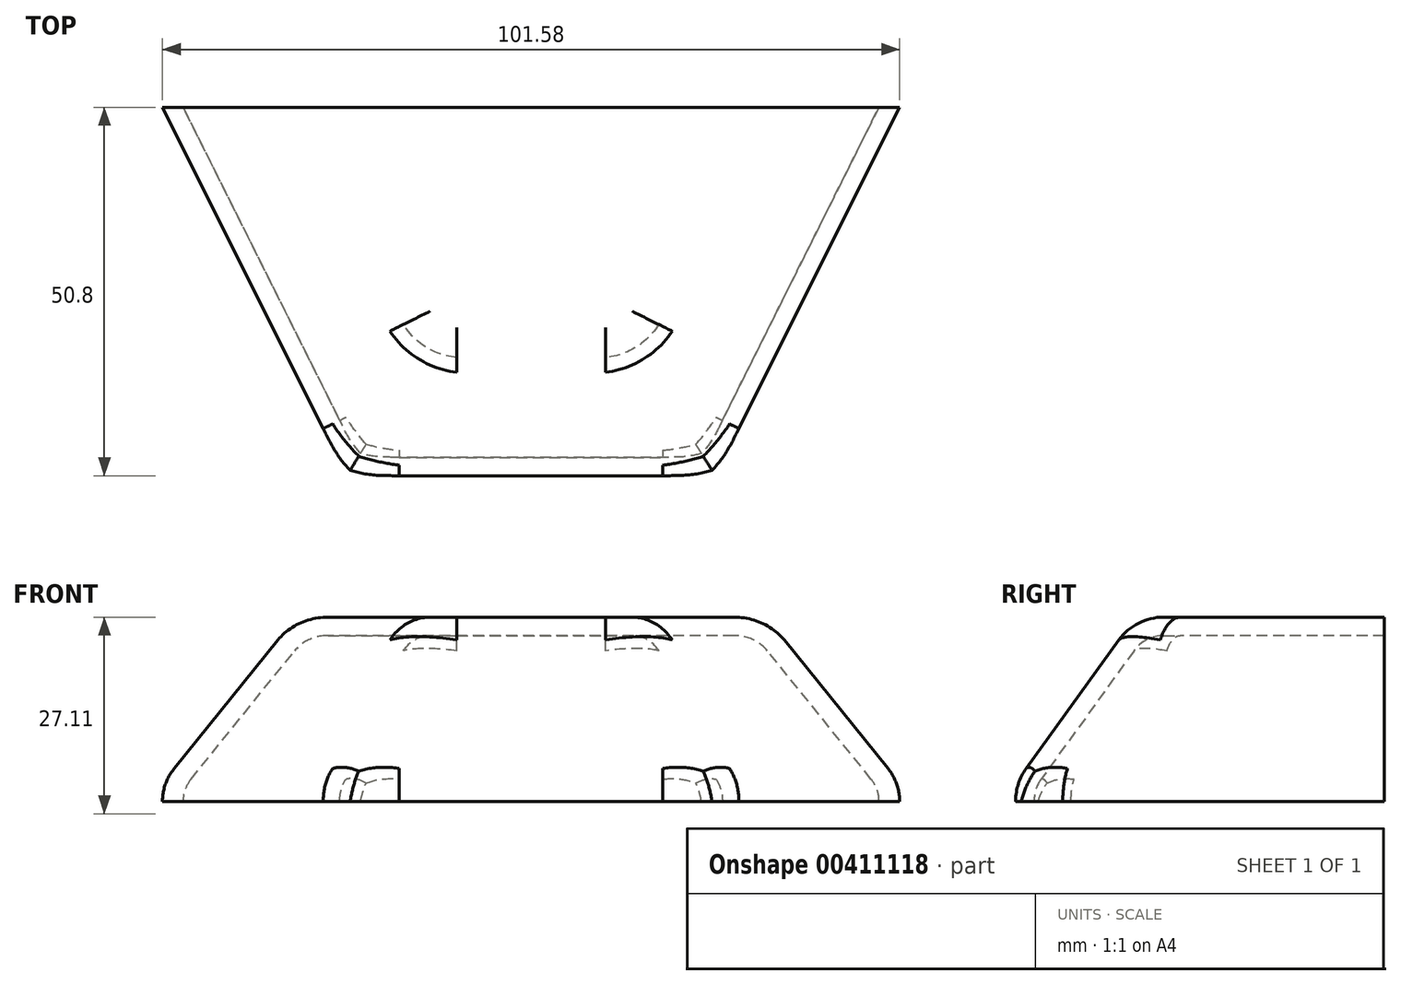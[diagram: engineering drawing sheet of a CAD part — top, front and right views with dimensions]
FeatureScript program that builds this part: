
annotation { "Feature Type Name" : "Feature", "Feature Type Description" : "" }
export const myFeature = defineFeature(function(context is Context, id is Id, definition is map)
    precondition{}
    {
        {
            var Q0;
            Q0=qCreatedBy(makeId("Top.planeOp"),FACE);
            var sketch = newSketch(context, id + "F0", { "sketchPlane" : qUnion([Q0])});
            skLineSegment(sketch, "E0.bottom", {"start": v(25.4, 25.4) * mm, "end": v(-25.4, 25.4) * mm});
            skLineSegment(sketch, "E0.top", {"start": v(25.4, -25.4) * mm, "end": v(-25.4, -25.4) * mm});
            skLineSegment(sketch, "E0.left", {"start": v(25.4, 25.4) * mm, "end": v(25.4, -25.4) * mm});
            skLineSegment(sketch, "E0.right", {"start": v(-25.4, 25.4) * mm, "end": v(-25.4, -25.4) * mm});
            skPoint(sketch, "E0.middle", {"position": v(0, 0) * mm});
            skLineSegment(sketch, "E1", {"start": v(25.4, 25.4) * mm, "end": v(50.79, 25.4) * mm});
            skLineSegment(sketch, "E2", {"start": v(50.79, 25.4) * mm, "end": v(25.4, -25.4) * mm});
            skLineSegment(sketch, "E3.MirrorCS", {"start": v(-25.4, 25.4) * mm, "end": v(-50.79, 25.4) * mm});
            skLineSegment(sketch, "E4.MirrorCS", {"start": v(-50.79, 25.4) * mm, "end": v(-25.4, -25.4) * mm});
            skSolve(sketch);
        }
        {
            var Q0;
            Q0=makeQuery(id+"F0.imprint","IMPRINT",FACE,{"disambiguationData":[TD([[makeQuery(id+"F0.imprint","IMPRINT",EDGE,{"derivedFrom":sQuery(id+"F0.wireOp",EDGE,"E0.right")}),-1.0]])]});
            var Q1;
            Q1=makeQuery(id+"F0.imprint","IMPRINT",FACE,{"disambiguationData":[TD([[makeQuery(id+"F0.imprint","IMPRINT",EDGE,{"derivedFrom":sQuery(id+"F0.wireOp",EDGE,"E0.bottom")}),1.0]])]});
            var Q2;
            Q2=makeQuery(id+"F0.imprint","IMPRINT",FACE,{"disambiguationData":[TD([[makeQuery(id+"F0.imprint","IMPRINT",EDGE,{"derivedFrom":sQuery(id+"F0.wireOp",EDGE,"E0.left")}),1.0]])]});
            extrude(context, id + "F1", {"entities" : qUnion([Q0, Q1, Q2]), "depth" : 25.4 * mm});
        }
        {
            var Q0;
            Q0=makeQuery(id+"F1.opExtrude","CAP_EDGE",EDGE,{"disambiguationData":[OSD([sQuery(id+"F0.wireOp",EDGE,"E4.MirrorCS")])],"isStart":false});
            var Q1;
            Q1=makeQuery(id+"F1.opExtrude","CAP_EDGE",EDGE,{"disambiguationData":[OSD([sQuery(id+"F0.wireOp",EDGE,"E0.top")])],"isStart":false});
            var Q2;
            Q2=makeQuery(id+"F1.opExtrude","CAP_EDGE",EDGE,{"disambiguationData":[OSD([sQuery(id+"F0.wireOp",EDGE,"E2")])],"isStart":false});
            chamfer(context, id + "F2", {"entities" : qUnion([Q0, Q1, Q2]), "chamferType" : ChamferType.TWO_OFFSETS, "width1" : 16.5 * mm, "oppositeDirection" : false, "width2" : 22.86 * mm, "tangentPropagation" : true});
        }
        {
            var Q0;
            Q0=makeQuery(id+"F2.opChamfer","BLEND_EDGE",EDGE,{"blendedFrom":[makeQuery(id+"F1.opExtrude","CAP_EDGE",EDGE,{"disambiguationData":[OSD([sQuery(id+"F0.wireOp",EDGE,"E0.top")])],"isStart":false}),makeQuery(id+"F1.opExtrude","CAP_EDGE",EDGE,{"disambiguationData":[OSD([sQuery(id+"F0.wireOp",EDGE,"E4.MirrorCS")])],"isStart":false})],"blendedInto":[]});
            var Q1;
            Q1=makeQuery(id+"F2.opChamfer","BLEND_EDGE",EDGE,{"blendedFrom":[makeQuery(id+"F1.opExtrude","CAP_EDGE",EDGE,{"disambiguationData":[OSD([sQuery(id+"F0.wireOp",EDGE,"E0.top")])],"isStart":false}),makeQuery(id+"F1.opExtrude","CAP_EDGE",EDGE,{"disambiguationData":[OSD([sQuery(id+"F0.wireOp",EDGE,"E2")])],"isStart":false})],"blendedInto":[]});
            fillet(context, id + "F3", {"entities" : qUnion([Q0, Q1]), "radius" : 12.7 * mm, "tangentPropagation" : true, "allowEdgeOverflow" : false});
        }
        {
            var Q0;
            {var subQ0=sQuery(id+"F0.wireOp",EDGE,"E4.MirrorCS");Q0=makeQuery(id+"F2.opChamfer","BLEND_EDGE",EDGE,{"blendedFrom":[makeQuery(id+"F1.opExtrude","CAP_EDGE",EDGE,{"disambiguationData":[OSD([subQ0])],"isStart":false}),makeQuery(id+"F1.opExtrude","SWEPT_FACE",FACE,{"disambiguationData":[OSD([subQ0])]})],"blendedInto":[makeQuery(id+"F1.opExtrude","SWEPT_FACE",FACE,{"disambiguationData":[OSD([subQ0])]})]});}
            var Q1;
            {var subQ0=sQuery(id+"F0.wireOp",EDGE,"E0.top");Q1=makeQuery(id+"F2.opChamfer","BLEND_EDGE",EDGE,{"blendedFrom":[makeQuery(id+"F1.opExtrude","CAP_EDGE",EDGE,{"disambiguationData":[OSD([subQ0])],"isStart":false}),makeQuery(id+"F1.opExtrude","SWEPT_FACE",FACE,{"disambiguationData":[OSD([subQ0])]})],"blendedInto":[makeQuery(id+"F1.opExtrude","SWEPT_FACE",FACE,{"disambiguationData":[OSD([subQ0])]})]});}
            var Q2;
            {var subQ0=sQuery(id+"F0.wireOp",EDGE,"E2");Q2=makeQuery(id+"F2.opChamfer","BLEND_EDGE",EDGE,{"blendedFrom":[makeQuery(id+"F1.opExtrude","CAP_EDGE",EDGE,{"disambiguationData":[OSD([subQ0])],"isStart":false}),makeQuery(id+"F1.opExtrude","SWEPT_FACE",FACE,{"disambiguationData":[OSD([subQ0])]})],"blendedInto":[makeQuery(id+"F1.opExtrude","SWEPT_FACE",FACE,{"disambiguationData":[OSD([subQ0])]})]});}
            fillet(context, id + "F4", {"entities" : qUnion([Q0, Q1, Q2]), "radius" : 7.62 * mm, "tangentPropagation" : true, "allowEdgeOverflow" : false});
        }
        {
            var Q0;
            {var subQ0=sQuery(id+"F0.wireOp",EDGE,"E4.MirrorCS");Q0=makeQuery(id+"F2.opChamfer","BLEND_EDGE",EDGE,{"blendedFrom":[makeQuery(id+"F1.opExtrude","CAP_EDGE",EDGE,{"disambiguationData":[OSD([subQ0])],"isStart":false}),makeQuery(id+"F1.opExtrude","CAP_FACE",FACE,{"disambiguationData":[OSD([sQuery(id+"F0.wireOp",EDGE,"E0.bottom"),sQuery(id+"F0.wireOp",EDGE,"E0.top"),sQuery(id+"F0.wireOp",EDGE,"E1"),sQuery(id+"F0.wireOp",EDGE,"E2"),sQuery(id+"F0.wireOp",EDGE,"E3.MirrorCS"),subQ0])],"isStart":false})],"blendedInto":[makeQuery(id+"F1.opExtrude","CAP_FACE",FACE,{"disambiguationData":[OSD([sQuery(id+"F0.wireOp",EDGE,"E0.bottom"),sQuery(id+"F0.wireOp",EDGE,"E0.top"),sQuery(id+"F0.wireOp",EDGE,"E1"),sQuery(id+"F0.wireOp",EDGE,"E2"),sQuery(id+"F0.wireOp",EDGE,"E3.MirrorCS"),subQ0])],"isStart":false})]});}
            var Q1;
            {var subQ0=sQuery(id+"F0.wireOp",EDGE,"E0.top");Q1=makeQuery(id+"F2.opChamfer","BLEND_EDGE",EDGE,{"blendedFrom":[makeQuery(id+"F1.opExtrude","CAP_EDGE",EDGE,{"disambiguationData":[OSD([subQ0])],"isStart":false}),makeQuery(id+"F1.opExtrude","CAP_FACE",FACE,{"disambiguationData":[OSD([sQuery(id+"F0.wireOp",EDGE,"E0.bottom"),subQ0,sQuery(id+"F0.wireOp",EDGE,"E1"),sQuery(id+"F0.wireOp",EDGE,"E2"),sQuery(id+"F0.wireOp",EDGE,"E3.MirrorCS"),sQuery(id+"F0.wireOp",EDGE,"E4.MirrorCS")])],"isStart":false})],"blendedInto":[makeQuery(id+"F1.opExtrude","CAP_FACE",FACE,{"disambiguationData":[OSD([sQuery(id+"F0.wireOp",EDGE,"E0.bottom"),subQ0,sQuery(id+"F0.wireOp",EDGE,"E1"),sQuery(id+"F0.wireOp",EDGE,"E2"),sQuery(id+"F0.wireOp",EDGE,"E3.MirrorCS"),sQuery(id+"F0.wireOp",EDGE,"E4.MirrorCS")])],"isStart":false})]});}
            var Q2;
            {var subQ0=sQuery(id+"F0.wireOp",EDGE,"E2");Q2=makeQuery(id+"F2.opChamfer","BLEND_EDGE",EDGE,{"blendedFrom":[makeQuery(id+"F1.opExtrude","CAP_EDGE",EDGE,{"disambiguationData":[OSD([subQ0])],"isStart":false}),makeQuery(id+"F1.opExtrude","CAP_FACE",FACE,{"disambiguationData":[OSD([sQuery(id+"F0.wireOp",EDGE,"E0.bottom"),sQuery(id+"F0.wireOp",EDGE,"E0.top"),sQuery(id+"F0.wireOp",EDGE,"E1"),subQ0,sQuery(id+"F0.wireOp",EDGE,"E3.MirrorCS"),sQuery(id+"F0.wireOp",EDGE,"E4.MirrorCS")])],"isStart":false})],"blendedInto":[makeQuery(id+"F1.opExtrude","CAP_FACE",FACE,{"disambiguationData":[OSD([sQuery(id+"F0.wireOp",EDGE,"E0.bottom"),sQuery(id+"F0.wireOp",EDGE,"E0.top"),sQuery(id+"F0.wireOp",EDGE,"E1"),subQ0,sQuery(id+"F0.wireOp",EDGE,"E3.MirrorCS"),sQuery(id+"F0.wireOp",EDGE,"E4.MirrorCS")])],"isStart":false})]});}
            fillet(context, id + "F5", {"entities" : qUnion([Q0, Q1, Q2]), "radius" : 7.62 * mm, "tangentPropagation" : true, "allowEdgeOverflow" : false});
        }
        {
            var Q0;
            Q0=makeQuery(id+"F1.opExtrude","CAP_FACE",FACE,{"disambiguationData":[OSD([sQuery(id+"F0.wireOp",EDGE,"E0.bottom"),sQuery(id+"F0.wireOp",EDGE,"E0.top"),sQuery(id+"F0.wireOp",EDGE,"E1"),sQuery(id+"F0.wireOp",EDGE,"E2"),sQuery(id+"F0.wireOp",EDGE,"E3.MirrorCS"),sQuery(id+"F0.wireOp",EDGE,"E4.MirrorCS")])],"isStart":true});
            var Q1;
            Q1=makeQuery(id+"F1.opExtrude","SWEPT_FACE",FACE,{"disambiguationData":[OSD([sQuery(id+"F0.wireOp",EDGE,"E0.bottom"),sQuery(id+"F0.wireOp",EDGE,"E1"),sQuery(id+"F0.wireOp",EDGE,"E3.MirrorCS")])]});
            shell(context, id + "F6", {"entities" : qUnion([Q0, Q1]), "thickness" : 2.54 * mm});
        }
    });
